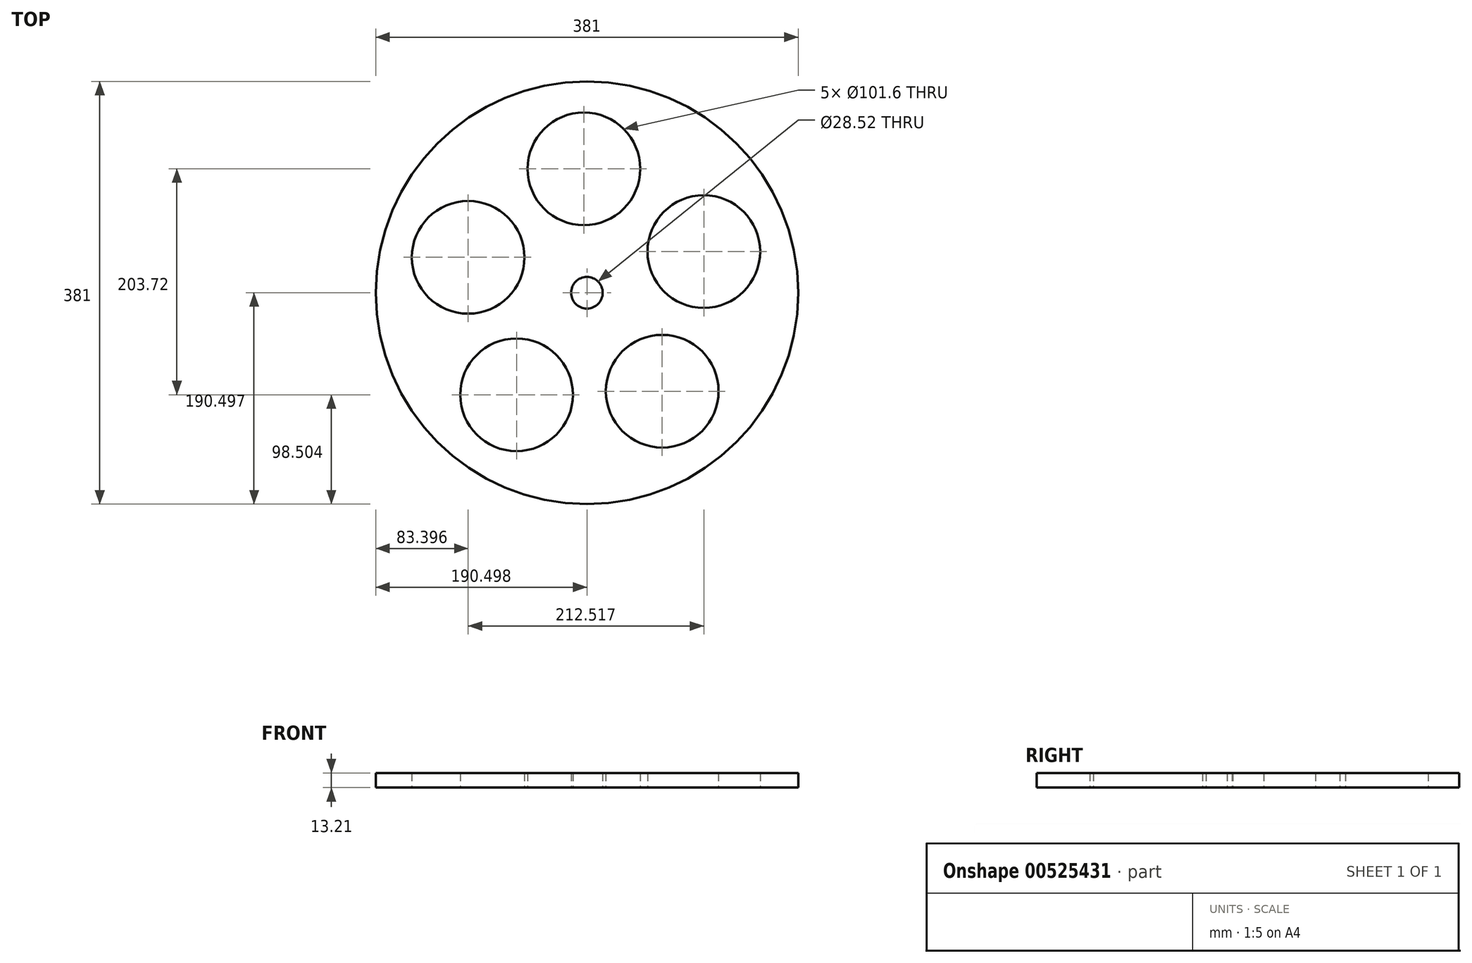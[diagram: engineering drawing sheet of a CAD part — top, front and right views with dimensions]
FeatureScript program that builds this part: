
annotation { "Feature Type Name" : "Feature", "Feature Type Description" : "" }
export const myFeature = defineFeature(function(context is Context, id is Id, definition is map)
    precondition{}
    {
        {
            var Q0;
            Q0=qCreatedBy(makeId("Top.planeOp"),FACE);
            var sketch = newSketch(context, id + "F0", { "sketchPlane" : qUnion([Q0])});
            skCircle(sketch, "E0", {"center": v(-63.96, -67.1) * mm, "radius": 190.5 * mm});
            skCircle(sketch, "E1", {"center": v(-66.7, 44.63) * mm, "radius": 50.8 * mm});
            skCircle(sketch, "E2.1.0", {"center": v(-171.06, -35.16) * mm, "radius": 50.8 * mm});
            skCircle(sketch, "E2.2.0", {"center": v(-127.43, -159.09) * mm, "radius": 50.8 * mm});
            skCircle(sketch, "E2.3.0", {"center": v(3.92, -155.88) * mm, "radius": 50.8 * mm});
            skCircle(sketch, "E2.4.0", {"center": v(41.45, -29.97) * mm, "radius": 50.8 * mm});
            skCircle(sketch, "E3", {"center": v(-63.96, -67.1) * mm, "radius": 14.26 * mm});
            skSolve(sketch);
        }
        {
            var Q0;
            Q0 = qSketchRegion(id + "F0", true);
            extrude(context, id + "F1", {"entities" : qUnion([Q0]), "depth" : 13.2 * mm, "offsetDistance" : 25.4 * mm});
        }
    });
